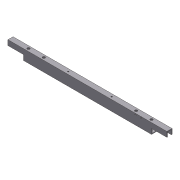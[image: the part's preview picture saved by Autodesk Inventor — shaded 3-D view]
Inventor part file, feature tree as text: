
AUTODESK INVENTOR PART (.ipt)
format: ipt  version: 2012 (Build 160160000, 160)  size: 180,736 bytes
history: native  units: in
note: dims shown in document units (in); Inventor stores cm internally (conversion verified against a paired STEP export)
features: extrude x8, sketch x8, shell x1
ambient origin geometry x8: Origin, YZ Plane, XZ Plane, XY Plane, X Axis, Y Axis, Z Axis, Center Point
bodies: Solid1 (feature_tree)
feature tree (17):
  extrude  "Extrusion1"  Depth=2.0in
  shell  "Shell1"  Thickness=31.0in
  extrude  "Extrusion2"  Depth=0.125in
  extrude  "Extrusion4"  Depth=1.0in TaperAngle=0.0deg
  extrude  "Extrusion5"  Depth=11.25in
  extrude  "Extrusion6"  Depth=0.5in
  extrude  "Extrusion7"  Depth=0.25in
  extrude  "Extrusion8"  Depth=1.0in TaperAngle=0.0deg
  extrude  "Extrusion9"  Depth=0.5in
  sketch  "Sketch1"  dims[d2=2.0in d3=2.0in d4=31.0in]
  sketch  "Sketch2"  dims[d6=1.0in d7=0.0in d8=0.125in]
  sketch  "Sketch4"  dims[d9=1.0in d10=1.0in d11=0.0in]
  sketch  "Sketch5"  dims[d12=3.0in d21=11.25in]
  sketch  "Sketch6"  dims[d22=8.5in d23=0.5in]
  sketch  "Sketch7"  dims[d24=0.5in d25=0.25in]
  sketch  "Sketch8"  dims[d26=0.25in d27=1.0in d28=0.0in]
  sketch  "Sketch9"  dims[d29=0.5in d30=0.5in d31=1.0in d32=0.0in d33=3.4998in d34=3.0in d35=0.25in d36=0.5in d37=0.5in d38=0.5in d39=0.5in d40=3.4998in d41=3.0in d42=1.0in d43=0.0in d44=0.5in d45=1.0in d46=0.0in d47=5.0in d48=1.125in d49=0.625in d50=0.25in d51=1.0in d52=0.0in d53=5.0in d54=1.125in d55=18.75in d56=0.5in d57=1.0in d58=0.0in]
